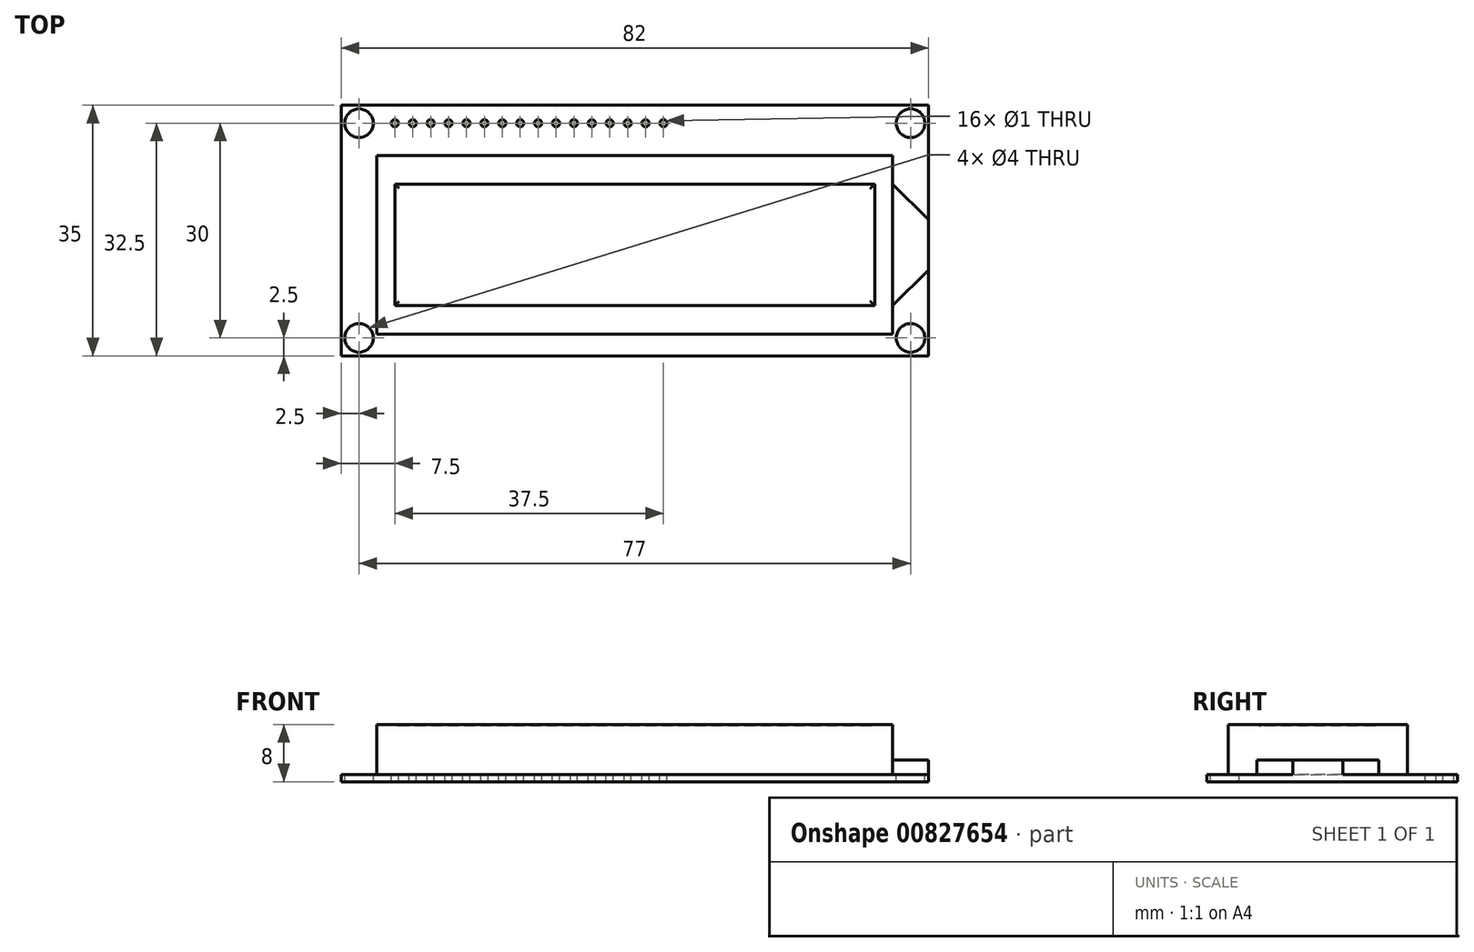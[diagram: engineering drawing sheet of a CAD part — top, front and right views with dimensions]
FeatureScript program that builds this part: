
annotation { "Feature Type Name" : "Feature", "Feature Type Description" : "" }
export const myFeature = defineFeature(function(context is Context, id is Id, definition is map)
    precondition{}
    {
        {
            var Q0;
            Q0=qCreatedBy(makeId("Top.planeOp"),FACE);
            var sketch = newSketch(context, id + "F0", { "sketchPlane" : qUnion([Q0])});
            skLineSegment(sketch, "E0.bottom", {"start": v(41, 17.5) * mm, "end": v(-41, 17.5) * mm});
            skLineSegment(sketch, "E0.top", {"start": v(41, -17.5) * mm, "end": v(-41, -17.5) * mm});
            skLineSegment(sketch, "E0.left", {"start": v(41, 17.5) * mm, "end": v(41, -17.5) * mm});
            skLineSegment(sketch, "E0.right", {"start": v(-41, 17.5) * mm, "end": v(-41, -17.5) * mm});
            skPoint(sketch, "E0.middle", {"position": v(0, 0) * mm});
            skSolve(sketch);
        }
        {
            var Q0;
            Q0=qSketchRegion(id+"F0",true);
            extrude(context, id + "F1", {"entities" : qUnion([Q0]), "depth" : 1 * mm, "offsetDistance" : 25 * mm});
        }
        {
            var Q0;
            Q0=makeQuery(id+"F1.opExtrude","CAP_FACE",FACE,{"disambiguationData":[OSD([sQuery(id+"F0.wireOp",EDGE,"E0.bottom"),sQuery(id+"F0.wireOp",EDGE,"E0.top"),sQuery(id+"F0.wireOp",EDGE,"E0.left"),sQuery(id+"F0.wireOp",EDGE,"E0.right")])],"isStart":false});
            var sketch = newSketch(context, id + "F2", { "sketchPlane" : qUnion([Q0])});
            skLineSegment(sketch, "E1.bottom", {"start": v(-36, -14.5) * mm, "end": v(36, -14.5) * mm});
            skLineSegment(sketch, "E1.top", {"start": v(-36, 10.5) * mm, "end": v(36, 10.5) * mm});
            skLineSegment(sketch, "E1.left", {"start": v(-36, -14.5) * mm, "end": v(-36, 10.5) * mm});
            skLineSegment(sketch, "E1.right", {"start": v(36, -14.5) * mm, "end": v(36, 10.5) * mm});
            skSolve(sketch);
        }
        {
            var Q0;
            Q0=qSketchRegion(id+"F2",true);
            extrude(context, id + "F3", {"entities" : qUnion([Q0]), "operationType" : NewBodyOperationType.ADD, "depth" : 7 * mm, "offsetDistance" : 25 * mm});
        }
        {
            var Q0;
            Q0=makeQuery(id+"F1.opExtrude","CAP_FACE",FACE,{"disambiguationData":[OSD([sQuery(id+"F0.wireOp",EDGE,"E0.bottom"),sQuery(id+"F0.wireOp",EDGE,"E0.top"),sQuery(id+"F0.wireOp",EDGE,"E0.left"),sQuery(id+"F0.wireOp",EDGE,"E0.right")])],"isStart":false});
            var sketch = newSketch(context, id + "F4", { "sketchPlane" : qUnion([Q0])});
            skLineSegment(sketch, "E2.left", {"start": v(41, -5.5) * mm, "end": v(41, 1.5) * mm});
            skLineSegment(sketch, "E3", {"start": v(36, -10.5) * mm, "end": v(41, -5.5) * mm});
            skLineSegment(sketch, "E4", {"start": v(41, 1.5) * mm, "end": v(36, 6.5) * mm});
            skLineSegment(sketch, "E5", {"start": v(36, 6.5) * mm, "end": v(36, -10.5) * mm});
            skSolve(sketch);
        }
        {
            var Q0;
            Q0=qSketchRegion(id+"F4",true);
            extrude(context, id + "F5", {"entities" : qUnion([Q0]), "operationType" : NewBodyOperationType.ADD, "depth" : 2 * mm, "offsetDistance" : 25 * mm});
        }
        {
            var Q0;
            Q0=makeQuery(id+"F1.opExtrude","CAP_FACE",FACE,{"disambiguationData":[OSD([sQuery(id+"F0.wireOp",EDGE,"E0.bottom"),sQuery(id+"F0.wireOp",EDGE,"E0.top"),sQuery(id+"F0.wireOp",EDGE,"E0.left"),sQuery(id+"F0.wireOp",EDGE,"E0.right")])],"isStart":false});
            var sketch = newSketch(context, id + "F6", { "sketchPlane" : qUnion([Q0])});
            skCircle(sketch, "E6", {"center": v(-38.5, -15) * mm, "radius": 2 * mm});
            skCircle(sketch, "E7.MirrorC", {"center": v(38.5, -15) * mm, "radius": 2 * mm});
            skCircle(sketch, "E8.MirrorC", {"center": v(-38.5, 15) * mm, "radius": 2 * mm});
            skCircle(sketch, "E9.MirrorC", {"center": v(38.5, 15) * mm, "radius": 2 * mm});
            skSolve(sketch);
        }
        {
            var Q0;
            Q0=qSketchRegion(id+"F6",true);
            extrude(context, id + "F7", {"entities" : qUnion([Q0]), "operationType" : NewBodyOperationType.REMOVE, "oppositeDirection" : true, "depth" : 2 * mm, "offsetDistance" : 25 * mm});
        }
        {
            var Q0;
            Q0=makeQuery(id+"F3.opExtrude","CAP_FACE",FACE,{"disambiguationData":[OSD([sQuery(id+"F2.wireOp",EDGE,"E1.bottom"),sQuery(id+"F2.wireOp",EDGE,"E1.top"),sQuery(id+"F2.wireOp",EDGE,"E1.left"),sQuery(id+"F2.wireOp",EDGE,"E1.right")])],"isStart":false});
            var sketch = newSketch(context, id + "F8", { "sketchPlane" : qUnion([Q0])});
            skLineSegment(sketch, "E10.bottom", {"start": v(33.5, 6.5) * mm, "end": v(-33.5, 6.5) * mm});
            skLineSegment(sketch, "E10.top", {"start": v(33.5, -10.5) * mm, "end": v(-33.5, -10.5) * mm});
            skLineSegment(sketch, "E10.left", {"start": v(33.5, 6.5) * mm, "end": v(33.5, -10.5) * mm});
            skLineSegment(sketch, "E10.right", {"start": v(-33.5, 6.5) * mm, "end": v(-33.5, -10.5) * mm});
            skSolve(sketch);
        }
        {
            var Q0;
            Q0=qSketchRegion(id+"F8",true);
            extrude(context, id + "F9", {"entities" : qUnion([Q0]), "operationType" : NewBodyOperationType.REMOVE, "oppositeDirection" : true, "depth" : 0.2 * mm, "offsetDistance" : 25 * mm});
        }
        {
            var Q0;
            Q0=makeQuery(id+"F9.boolean.opBoolean","COPY",FACE,{"derivedFrom":makeQuery(id+"F9.opExtrude","CAP_FACE",FACE,{"disambiguationData":[OSD([sQuery(id+"F8.wireOp",EDGE,"E10.bottom"),sQuery(id+"F8.wireOp",EDGE,"E10.top"),sQuery(id+"F8.wireOp",EDGE,"E10.left"),sQuery(id+"F8.wireOp",EDGE,"E10.right")])],"isStart":false})});
            fillet(context, id + "F10", {"entities" : qUnion([Q0]), "radius" : 1 * mm, "tangentPropagation" : true, "allowEdgeOverflow" : false});
        }
        {
            var Q0;
            Q0=makeQuery(id+"F1.opExtrude","CAP_FACE",FACE,{"disambiguationData":[OSD([sQuery(id+"F0.wireOp",EDGE,"E0.bottom"),sQuery(id+"F0.wireOp",EDGE,"E0.top"),sQuery(id+"F0.wireOp",EDGE,"E0.left"),sQuery(id+"F0.wireOp",EDGE,"E0.right")])],"isStart":false});
            var sketch = newSketch(context, id + "F11", { "sketchPlane" : qUnion([Q0])});
            skCircle(sketch, "E11", {"center": v(-33.5, 15) * mm, "radius": 0.5 * mm});
            skCircle(sketch, "E12.1.0.0", {"center": v(-31, 15) * mm, "radius": 0.5 * mm});
            skCircle(sketch, "E12.2.0.0", {"center": v(-28.5, 15) * mm, "radius": 0.5 * mm});
            skCircle(sketch, "E12.3.0.0", {"center": v(-26, 15) * mm, "radius": 0.5 * mm});
            skCircle(sketch, "E12.4.0.0", {"center": v(-23.5, 15) * mm, "radius": 0.5 * mm});
            skCircle(sketch, "E12.5.0.0", {"center": v(-21, 15) * mm, "radius": 0.5 * mm});
            skCircle(sketch, "E12.6.0.0", {"center": v(-18.5, 15) * mm, "radius": 0.5 * mm});
            skCircle(sketch, "E12.7.0.0", {"center": v(-16, 15) * mm, "radius": 0.5 * mm});
            skCircle(sketch, "E12.8.0.0", {"center": v(-13.5, 15) * mm, "radius": 0.5 * mm});
            skCircle(sketch, "E12.9.0.0", {"center": v(-11, 15) * mm, "radius": 0.5 * mm});
            skCircle(sketch, "E12.10.0.0", {"center": v(-8.5, 15) * mm, "radius": 0.5 * mm});
            skCircle(sketch, "E12.11.0.0", {"center": v(-6, 15) * mm, "radius": 0.5 * mm});
            skCircle(sketch, "E12.12.0.0", {"center": v(-3.5, 15) * mm, "radius": 0.5 * mm});
            skCircle(sketch, "E12.13.0.0", {"center": v(-1, 15) * mm, "radius": 0.5 * mm});
            skCircle(sketch, "E12.14.0.0", {"center": v(1.5, 15) * mm, "radius": 0.5 * mm});
            skCircle(sketch, "E12.15.0.0", {"center": v(4, 15) * mm, "radius": 0.5 * mm});
            skLineSegment(sketch, "E12.direction1", {"start": v(-33.5, 15) * mm, "end": v(-31, 15) * mm, "construction": true});
            skSolve(sketch);
        }
        {
            var Q0;
            Q0=qSketchRegion(id+"F11",true);
            extrude(context, id + "F12", {"entities" : qUnion([Q0]), "operationType" : NewBodyOperationType.REMOVE, "oppositeDirection" : true, "depth" : 2 * mm, "offsetDistance" : 25 * mm});
        }
    });
